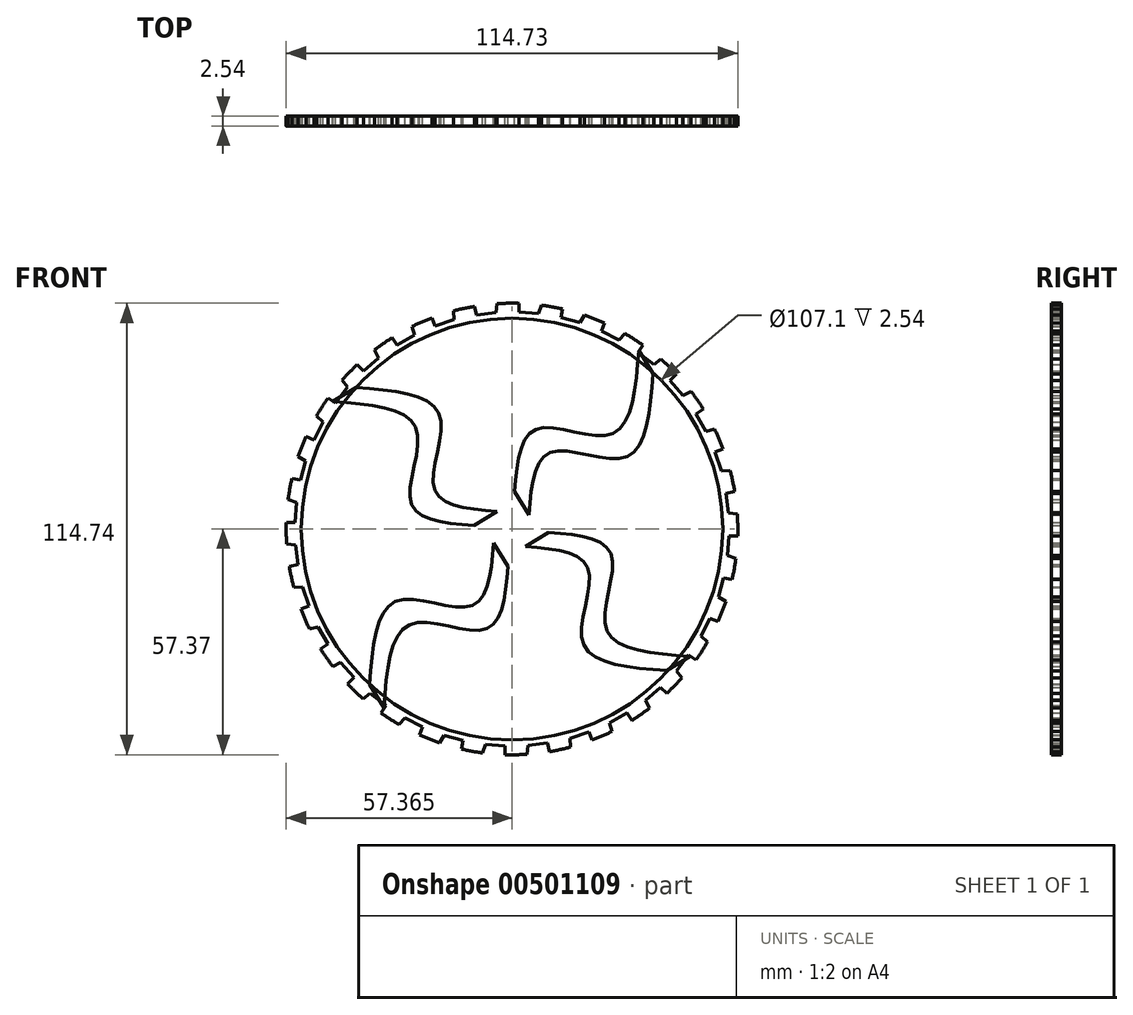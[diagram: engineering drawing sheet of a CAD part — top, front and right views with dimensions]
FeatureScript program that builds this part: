
annotation { "Feature Type Name" : "Feature", "Feature Type Description" : "" }
export const myFeature = defineFeature(function(context is Context, id is Id, definition is map)
    precondition{}
    {
        {
            var Q0;
            Q0=qCreatedBy(makeId("Front.planeOp"),FACE);
            var sketch = newSketch(context, id + "F0", { "sketchPlane" : qUnion([Q0])});
            skFitSpline(sketch, "E0", {"points": [v(10.5, 9.47) * mm, v(16.18, 25.42) * mm, v(35.06, 24.13) * mm, v(42.02, 45.4) * mm], "startDerivative": vector(5.76, 69.3) * mm, "endDerivative": vector(6.14, 80.76) * mm});
            skFitSpline(sketch, "E1", {"points": [v(14.1, 3.58) * mm, v(19.77, 19.52) * mm, v(38.65, 18.24) * mm, v(45.61, 39.5) * mm], "startDerivative": vector(5.76, 69.3) * mm, "endDerivative": vector(6.14, 80.76) * mm});
            skLineSegment(sketch, "E2", {"start": v(42.02, 45.4) * mm, "end": v(45.61, 39.5) * mm});
            skLineSegment(sketch, "E3", {"start": v(10.5, 9.47) * mm, "end": v(14.1, 3.58) * mm});
            skPoint(sketch, "E4", {"position": v(6.29, 2.88) * mm});
            skSolve(sketch);
        }
        {
            var Q0;
            Q0 = qSketchRegion(id + "F0", true);
            extrude(context, id + "F1", {"entities" : qUnion([Q0]), "depth" : 2.54 * mm});
        }
        {
            var Q0;
            Q0=qCreatedBy(makeId("Top.planeOp"),FACE);
            var sketch = newSketch(context, id + "F2", { "sketchPlane" : qUnion([Q0])});
            skLineSegment(sketch, "E5", {"start": v(9.64, -10.19) * mm, "end": v(9.64, 8.62) * mm});
            skSolve(sketch);
        }
        {
            var Q0;
            Q0=makeQuery(id+"F1.opExtrude","SWEPT_BODY",BODY,{"disambiguationData":[OSD([sQuery(id+"F0.wireOp",EDGE,"E0"),sQuery(id+"F0.wireOp",EDGE,"E1"),sQuery(id+"F0.wireOp",EDGE,"E2"),sQuery(id+"F0.wireOp",EDGE,"E3")])]});
            var Q1;
            Q1=sQuery(id+"F2.wireOp",EDGE,"E5");
            circularPattern(context, id + "F3", {"entities" : qUnion([Q0]), "axis" : qUnion([Q1]), "angle" : 360 * degree, "instanceCount" : 4, "equalSpace" : true});
        }
        {
            var Q0;
            Q0=qCreatedBy(makeId("Front.planeOp"),FACE);
            var sketch = newSketch(context, id + "F4", { "sketchPlane" : qUnion([Q0])});
            skCircle(sketch, "E6", {"center": v(9.82, 0) * mm, "radius": 53.55 * mm});
            skCircle(sketch, "E7", {"center": v(9.82, 0) * mm, "radius": 57.37 * mm});
            skLineSegment(sketch, "E8", {"start": v(11.54, 57.34) * mm, "end": v(11.54, 55.11) * mm});
            skLineSegment(sketch, "E9", {"start": v(11.54, 55.11) * mm, "end": v(16.57, 54.77) * mm});
            skLineSegment(sketch, "E10", {"start": v(16.57, 54.77) * mm, "end": v(17.3, 56.88) * mm});
            skLineSegment(sketch, "E11.1.0", {"start": v(0.32, 56.57) * mm, "end": v(0.76, 54.4) * mm});
            skLineSegment(sketch, "E11.1.1", {"start": v(0.76, 54.4) * mm, "end": v(5.76, 55.04) * mm});
            skLineSegment(sketch, "E11.1.2", {"start": v(5.76, 55.04) * mm, "end": v(6.06, 57.24) * mm});
            skLineSegment(sketch, "E11.2.0", {"start": v(-10.53, 53.63) * mm, "end": v(-9.68, 51.58) * mm});
            skLineSegment(sketch, "E11.2.1", {"start": v(-9.68, 51.58) * mm, "end": v(-4.9, 53.19) * mm});
            skLineSegment(sketch, "E11.2.2", {"start": v(-4.9, 53.19) * mm, "end": v(-5.04, 55.4) * mm});
            skLineSegment(sketch, "E11.3.0", {"start": v(-20.6, 48.63) * mm, "end": v(-19.37, 46.78) * mm});
            skLineSegment(sketch, "E11.3.1", {"start": v(-19.37, 46.78) * mm, "end": v(-15, 49.3) * mm});
            skLineSegment(sketch, "E11.3.2", {"start": v(-15, 49.3) * mm, "end": v(-15.56, 51.44) * mm});
            skLineSegment(sketch, "E11.4.0", {"start": v(-29.5, 41.76) * mm, "end": v(-27.93, 40.19) * mm});
            skLineSegment(sketch, "E11.4.1", {"start": v(-27.93, 40.19) * mm, "end": v(-24.13, 43.5) * mm});
            skLineSegment(sketch, "E11.4.2", {"start": v(-24.13, 43.5) * mm, "end": v(-25.11, 45.5) * mm});
            skLineSegment(sketch, "E11.5.0", {"start": v(-36.9, 33.28) * mm, "end": v(-35.05, 32.05) * mm});
            skLineSegment(sketch, "E11.5.1", {"start": v(-35.05, 32.05) * mm, "end": v(-31.97, 36.04) * mm});
            skLineSegment(sketch, "E11.5.2", {"start": v(-31.97, 36.04) * mm, "end": v(-33.32, 37.81) * mm});
            skLineSegment(sketch, "E11.6.0", {"start": v(-42.5, 23.53) * mm, "end": v(-40.44, 22.68) * mm});
            skLineSegment(sketch, "E11.6.1", {"start": v(-40.44, 22.68) * mm, "end": v(-38.2, 27.2) * mm});
            skLineSegment(sketch, "E11.6.2", {"start": v(-38.2, 27.2) * mm, "end": v(-39.86, 28.67) * mm});
            skLineSegment(sketch, "E11.7.0", {"start": v(-46.08, 12.87) * mm, "end": v(-43.9, 12.44) * mm});
            skLineSegment(sketch, "E11.7.1", {"start": v(-43.9, 12.44) * mm, "end": v(-42.58, 17.3) * mm});
            skLineSegment(sketch, "E11.7.2", {"start": v(-42.58, 17.3) * mm, "end": v(-44.5, 18.42) * mm});
            skLineSegment(sketch, "E11.8.0", {"start": v(-47.51, 1.72) * mm, "end": v(-45.29, 1.72) * mm});
            skLineSegment(sketch, "E11.8.1", {"start": v(-45.29, 1.72) * mm, "end": v(-44.95, 6.75) * mm});
            skLineSegment(sketch, "E11.8.2", {"start": v(-44.95, 6.75) * mm, "end": v(-47.05, 7.47) * mm});
            skLineSegment(sketch, "E11.9.0", {"start": v(-46.75, -9.5) * mm, "end": v(-44.57, -9.07) * mm});
            skLineSegment(sketch, "E11.9.1", {"start": v(-44.57, -9.07) * mm, "end": v(-45.21, -4.07) * mm});
            skLineSegment(sketch, "E11.9.2", {"start": v(-45.21, -4.07) * mm, "end": v(-47.42, -3.77) * mm});
            skLineSegment(sketch, "E11.10.0", {"start": v(-43.8, -20.36) * mm, "end": v(-41.75, -19.5) * mm});
            skLineSegment(sketch, "E11.10.1", {"start": v(-41.75, -19.5) * mm, "end": v(-43.36, -14.73) * mm});
            skLineSegment(sketch, "E11.10.2", {"start": v(-43.36, -14.73) * mm, "end": v(-45.58, -14.86) * mm});
            skLineSegment(sketch, "E11.11.0", {"start": v(-38.8, -30.43) * mm, "end": v(-36.95, -29.2) * mm});
            skLineSegment(sketch, "E11.11.1", {"start": v(-36.95, -29.2) * mm, "end": v(-39.47, -24.82) * mm});
            skLineSegment(sketch, "E11.11.2", {"start": v(-39.47, -24.82) * mm, "end": v(-41.62, -25.39) * mm});
            skLineSegment(sketch, "E11.12.0", {"start": v(-31.93, -39.33) * mm, "end": v(-30.36, -37.76) * mm});
            skLineSegment(sketch, "E11.12.1", {"start": v(-30.36, -37.76) * mm, "end": v(-33.68, -33.96) * mm});
            skLineSegment(sketch, "E11.12.2", {"start": v(-33.68, -33.96) * mm, "end": v(-35.68, -34.94) * mm});
            skLineSegment(sketch, "E11.13.0", {"start": v(-23.46, -46.72) * mm, "end": v(-22.22, -44.87) * mm});
            skLineSegment(sketch, "E11.13.1", {"start": v(-22.22, -44.87) * mm, "end": v(-26.22, -41.8) * mm});
            skLineSegment(sketch, "E11.13.2", {"start": v(-26.22, -41.8) * mm, "end": v(-27.99, -43.14) * mm});
            skLineSegment(sketch, "E11.14.0", {"start": v(-13.7, -52.32) * mm, "end": v(-12.85, -50.26) * mm});
            skLineSegment(sketch, "E11.14.1", {"start": v(-12.85, -50.26) * mm, "end": v(-17.37, -48.02) * mm});
            skLineSegment(sketch, "E11.14.2", {"start": v(-17.37, -48.02) * mm, "end": v(-18.84, -49.69) * mm});
            skLineSegment(sketch, "E11.15.0", {"start": v(-3.05, -55.9) * mm, "end": v(-2.61, -53.72) * mm});
            skLineSegment(sketch, "E11.15.1", {"start": v(-2.61, -53.72) * mm, "end": v(-7.48, -52.4) * mm});
            skLineSegment(sketch, "E11.15.2", {"start": v(-7.48, -52.4) * mm, "end": v(-8.6, -54.33) * mm});
            skLineSegment(sketch, "E11.16.0", {"start": v(8.1, -57.34) * mm, "end": v(8.1, -55.11) * mm});
            skLineSegment(sketch, "E11.16.1", {"start": v(8.1, -55.11) * mm, "end": v(3.08, -54.77) * mm});
            skLineSegment(sketch, "E11.16.2", {"start": v(3.08, -54.77) * mm, "end": v(2.35, -56.88) * mm});
            skLineSegment(sketch, "E11.17.0", {"start": v(19.33, -56.57) * mm, "end": v(18.9, -54.4) * mm});
            skLineSegment(sketch, "E11.17.1", {"start": v(18.9, -54.4) * mm, "end": v(13.9, -55.04) * mm});
            skLineSegment(sketch, "E11.17.2", {"start": v(13.9, -55.04) * mm, "end": v(13.6, -57.24) * mm});
            skLineSegment(sketch, "E11.18.0", {"start": v(30.18, -53.63) * mm, "end": v(29.33, -51.58) * mm});
            skLineSegment(sketch, "E11.18.1", {"start": v(29.33, -51.58) * mm, "end": v(24.55, -53.19) * mm});
            skLineSegment(sketch, "E11.18.2", {"start": v(24.55, -53.19) * mm, "end": v(24.69, -55.4) * mm});
            skLineSegment(sketch, "E11.19.0", {"start": v(40.25, -48.63) * mm, "end": v(39.02, -46.78) * mm});
            skLineSegment(sketch, "E11.19.1", {"start": v(39.02, -46.78) * mm, "end": v(34.64, -49.3) * mm});
            skLineSegment(sketch, "E11.19.2", {"start": v(34.64, -49.3) * mm, "end": v(35.21, -51.44) * mm});
            skLineSegment(sketch, "E11.20.0", {"start": v(49.16, -41.76) * mm, "end": v(47.58, -40.19) * mm});
            skLineSegment(sketch, "E11.20.1", {"start": v(47.58, -40.19) * mm, "end": v(43.78, -43.5) * mm});
            skLineSegment(sketch, "E11.20.2", {"start": v(43.78, -43.5) * mm, "end": v(44.76, -45.5) * mm});
            skLineSegment(sketch, "E11.21.0", {"start": v(56.55, -33.28) * mm, "end": v(54.7, -32.05) * mm});
            skLineSegment(sketch, "E11.21.1", {"start": v(54.7, -32.05) * mm, "end": v(51.62, -36.04) * mm});
            skLineSegment(sketch, "E11.21.2", {"start": v(51.62, -36.04) * mm, "end": v(52.97, -37.81) * mm});
            skLineSegment(sketch, "E11.22.0", {"start": v(62.14, -23.53) * mm, "end": v(60.09, -22.68) * mm});
            skLineSegment(sketch, "E11.22.1", {"start": v(60.09, -22.68) * mm, "end": v(57.85, -27.2) * mm});
            skLineSegment(sketch, "E11.22.2", {"start": v(57.85, -27.2) * mm, "end": v(59.51, -28.67) * mm});
            skLineSegment(sketch, "E11.23.0", {"start": v(65.73, -12.87) * mm, "end": v(63.55, -12.44) * mm});
            skLineSegment(sketch, "E11.23.1", {"start": v(63.55, -12.44) * mm, "end": v(62.23, -17.3) * mm});
            skLineSegment(sketch, "E11.23.2", {"start": v(62.23, -17.3) * mm, "end": v(64.15, -18.42) * mm});
            skLineSegment(sketch, "E11.24.0", {"start": v(67.16, -1.72) * mm, "end": v(64.94, -1.72) * mm});
            skLineSegment(sketch, "E11.24.1", {"start": v(64.94, -1.72) * mm, "end": v(64.6, -6.75) * mm});
            skLineSegment(sketch, "E11.24.2", {"start": v(64.6, -6.75) * mm, "end": v(66.7, -7.47) * mm});
            skLineSegment(sketch, "E11.25.0", {"start": v(66.4, 9.5) * mm, "end": v(64.22, 9.07) * mm});
            skLineSegment(sketch, "E11.25.1", {"start": v(64.22, 9.07) * mm, "end": v(64.86, 4.07) * mm});
            skLineSegment(sketch, "E11.25.2", {"start": v(64.86, 4.07) * mm, "end": v(67.07, 3.77) * mm});
            skLineSegment(sketch, "E11.26.0", {"start": v(63.46, 20.36) * mm, "end": v(61.4, 19.5) * mm});
            skLineSegment(sketch, "E11.26.1", {"start": v(61.4, 19.5) * mm, "end": v(63.01, 14.73) * mm});
            skLineSegment(sketch, "E11.26.2", {"start": v(63.01, 14.73) * mm, "end": v(65.23, 14.86) * mm});
            skLineSegment(sketch, "E11.27.0", {"start": v(58.45, 30.43) * mm, "end": v(56.6, 29.2) * mm});
            skLineSegment(sketch, "E11.27.1", {"start": v(56.6, 29.2) * mm, "end": v(59.12, 24.82) * mm});
            skLineSegment(sketch, "E11.27.2", {"start": v(59.12, 24.82) * mm, "end": v(61.27, 25.39) * mm});
            skLineSegment(sketch, "E11.28.0", {"start": v(51.58, 39.33) * mm, "end": v(50.01, 37.76) * mm});
            skLineSegment(sketch, "E11.28.1", {"start": v(50.01, 37.76) * mm, "end": v(53.33, 33.96) * mm});
            skLineSegment(sketch, "E11.28.2", {"start": v(53.33, 33.96) * mm, "end": v(55.33, 34.94) * mm});
            skLineSegment(sketch, "E11.29.0", {"start": v(43.1, 46.72) * mm, "end": v(41.87, 44.87) * mm});
            skLineSegment(sketch, "E11.29.1", {"start": v(41.87, 44.87) * mm, "end": v(45.87, 41.8) * mm});
            skLineSegment(sketch, "E11.29.2", {"start": v(45.87, 41.8) * mm, "end": v(47.64, 43.14) * mm});
            skLineSegment(sketch, "E11.30.0", {"start": v(33.35, 52.32) * mm, "end": v(32.5, 50.26) * mm});
            skLineSegment(sketch, "E11.30.1", {"start": v(32.5, 50.26) * mm, "end": v(37.02, 48.02) * mm});
            skLineSegment(sketch, "E11.30.2", {"start": v(37.02, 48.02) * mm, "end": v(38.5, 49.69) * mm});
            skLineSegment(sketch, "E11.31.0", {"start": v(22.7, 55.9) * mm, "end": v(22.26, 53.72) * mm});
            skLineSegment(sketch, "E11.31.1", {"start": v(22.26, 53.72) * mm, "end": v(27.13, 52.4) * mm});
            skLineSegment(sketch, "E11.31.2", {"start": v(27.13, 52.4) * mm, "end": v(28.25, 54.33) * mm});
            skSolve(sketch);
        }
        {
            var Q0;
            Q0=makeQuery(id+"F4.imprint","IMPRINT",FACE,{"disambiguationData":[TD([[makeQuery(id+"F4.imprint","IMPRINT",EDGE,{"derivedFrom":sQuery(id+"F4.wireOp",EDGE,"E6")}),-1.0]])]});
            extrude(context, id + "F5", {"entities" : qUnion([Q0]), "depth" : 2.54 * mm});
        }
    });
